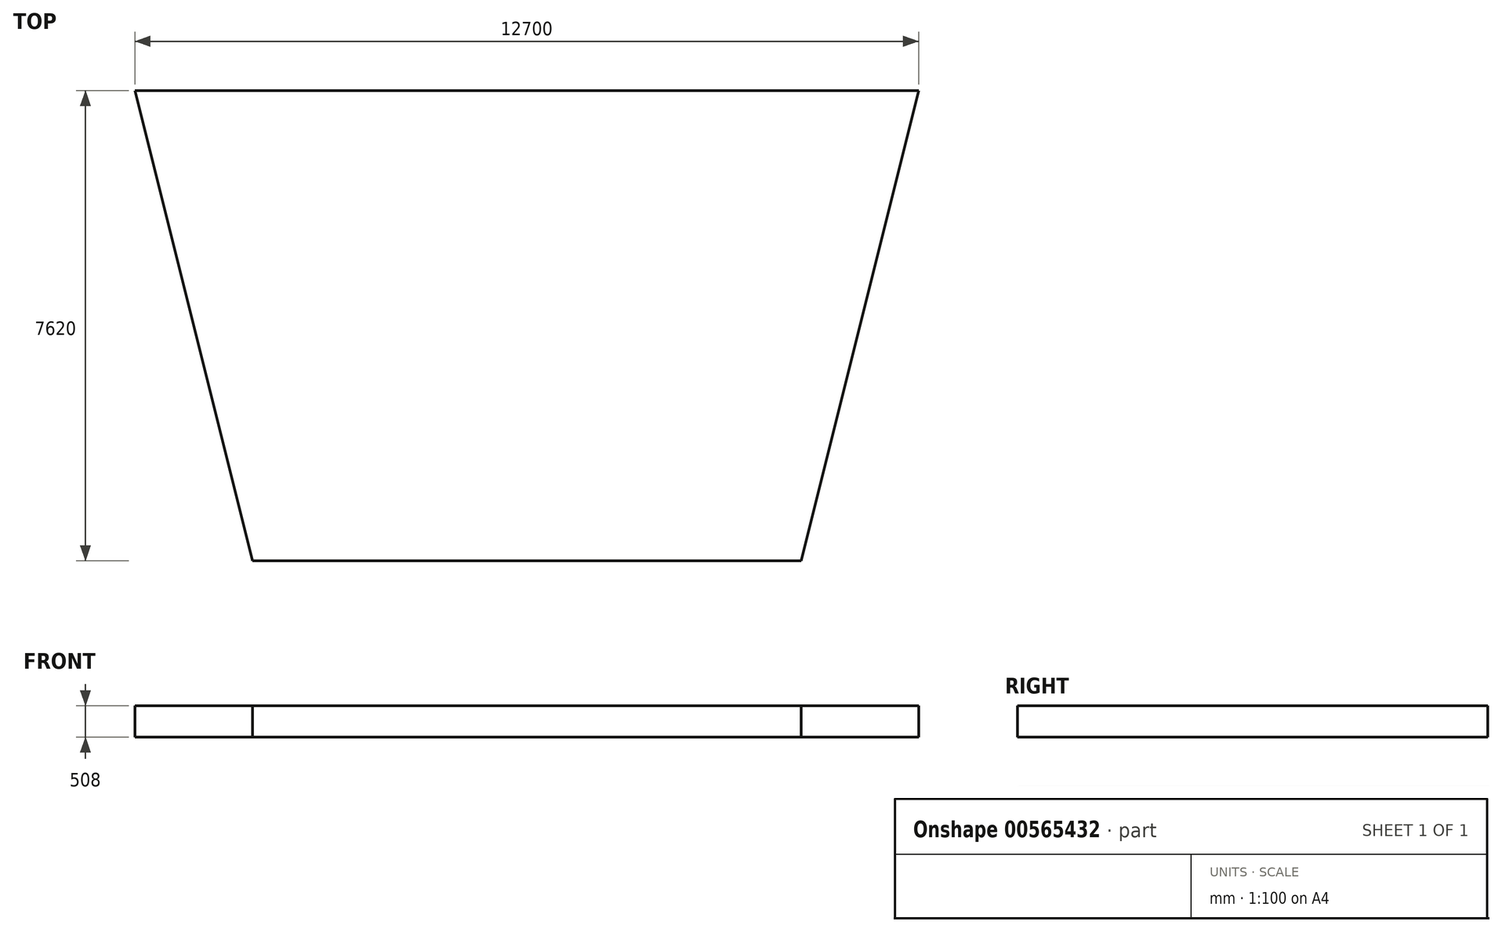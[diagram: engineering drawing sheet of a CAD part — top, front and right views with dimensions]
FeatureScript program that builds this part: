
annotation { "Feature Type Name" : "Feature", "Feature Type Description" : "" }
export const myFeature = defineFeature(function(context is Context, id is Id, definition is map)
    precondition{}
    {
        {
            var Q0;
            Q0=qCreatedBy(makeId("Top.planeOp"),FACE);
            var sketch = newSketch(context, id + "F0", { "sketchPlane" : qUnion([Q0])});
            skLineSegment(sketch, "E0", {"start": v(-4445, 0) * mm, "end": v(4445, 0) * mm});
            skLineSegment(sketch, "E1", {"start": v(4445, 0) * mm, "end": v(6350, 7620) * mm});
            skLineSegment(sketch, "E2", {"start": v(6350, 7620) * mm, "end": v(-6350, 7620) * mm});
            skLineSegment(sketch, "E3", {"start": v(-6350, 7620) * mm, "end": v(-4445, 0) * mm});
            skSolve(sketch);
        }
        {
            var Q0;
            Q0=makeQuery(id+"F0.imprint","IMPRINT",FACE,{"disambiguationData":[TD([[makeQuery(id+"F0.imprint","IMPRINT",EDGE,{"derivedFrom":sQuery(id+"F0.wireOp",EDGE,"E0")}),1.0]])]});
            extrude(context, id + "F1", {"entities" : qUnion([Q0]), "depth" : 508 * mm, "offsetDistance" : 25.4 * mm});
        }
    });
